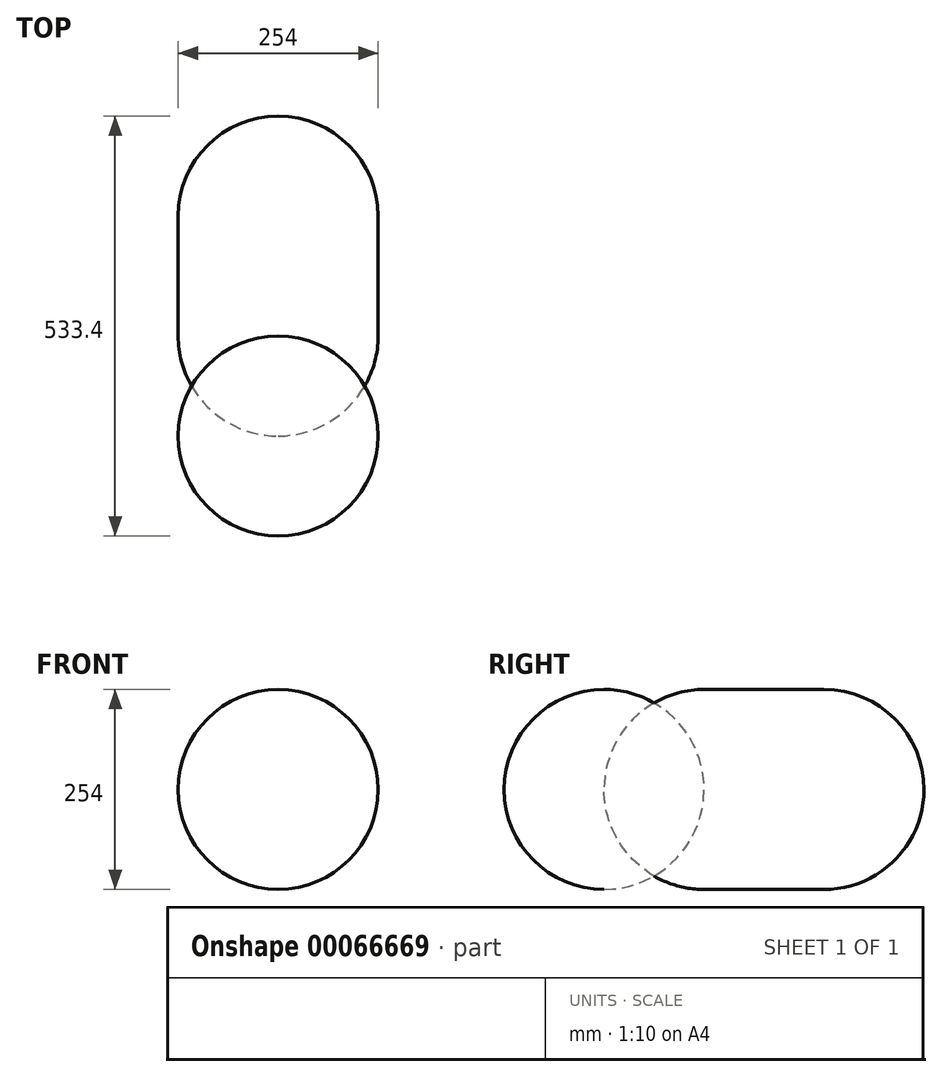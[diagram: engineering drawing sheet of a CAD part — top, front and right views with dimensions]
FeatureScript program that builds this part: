
annotation { "Feature Type Name" : "Feature", "Feature Type Description" : "" }
export const myFeature = defineFeature(function(context is Context, id is Id, definition is map)
    precondition{}
    {
        {
            var Q0;
            Q0=qCreatedBy(makeId("Front.planeOp"),FACE);
            var sketch = newSketch(context, id + "F0", { "sketchPlane" : qUnion([Q0])});
            skCircle(sketch, "E0", {"center": v(0, 0) * mm, "radius": 127 * mm});
            skLineSegment(sketch, "E1", {"start": v(0, 127) * mm, "end": v(0, -127) * mm});
            skSolve(sketch);
        }
        {
            var Q0;
            {var subQ0=sQuery(id+"F0.wireOp",EDGE,"E1");Q0=makeQuery(id+"F0.imprint","IMPRINT",FACE,{"disambiguationData":[TD([[makeQuery(id+"F0.imprint","IMPRINT",EDGE,{"derivedFrom":subQ0}),1.0]])]});}
            var Q1;
            Q1=sQuery(id+"F0.wireOp",EDGE,"E1");
            revolve(context, id + "F1", {"entities" : qUnion([Q0]), "axis" : qUnion([Q1]), "revolveType" : RevolveType.FULL});
        }
        {
            var Q0;
            {var subQ0=sQuery(id+"F0.wireOp",EDGE,"E1");Q0=makeQuery(id+"F0.imprint","IMPRINT",FACE,{"disambiguationData":[TD([[makeQuery(id+"F0.imprint","IMPRINT",EDGE,{"derivedFrom":subQ0}),-1.0]])]});}
            var Q1;
            {var subQ0=sQuery(id+"F0.wireOp",EDGE,"E1");Q1=makeQuery(id+"F0.imprint","IMPRINT",FACE,{"disambiguationData":[TD([[makeQuery(id+"F0.imprint","IMPRINT",EDGE,{"derivedFrom":subQ0}),1.0]])]});}
            extrude(context, id + "F2", {"entities" : qUnion([Q0, Q1]), "oppositeDirection" : true, "depth" : 406.4 * mm});
        }
        {
            var Q0;
            Q0=makeQuery(id+"F2.opExtrude","CAP_FACE",FACE,{"disambiguationData":[OSD([sQuery(id+"F0.wireOp",EDGE,"E0")])],"isStart":true});
            var Q1;
            Q1=makeQuery(id+"F2.opExtrude","CAP_FACE",FACE,{"disambiguationData":[OSD([sQuery(id+"F0.wireOp",EDGE,"E0")])],"isStart":false});
            fillet(context, id + "F3", {"entities" : qUnion([Q0, Q1]), "radius" : 127 * mm, "tangentPropagation" : true, "allowEdgeOverflow" : false});
        }
    });
